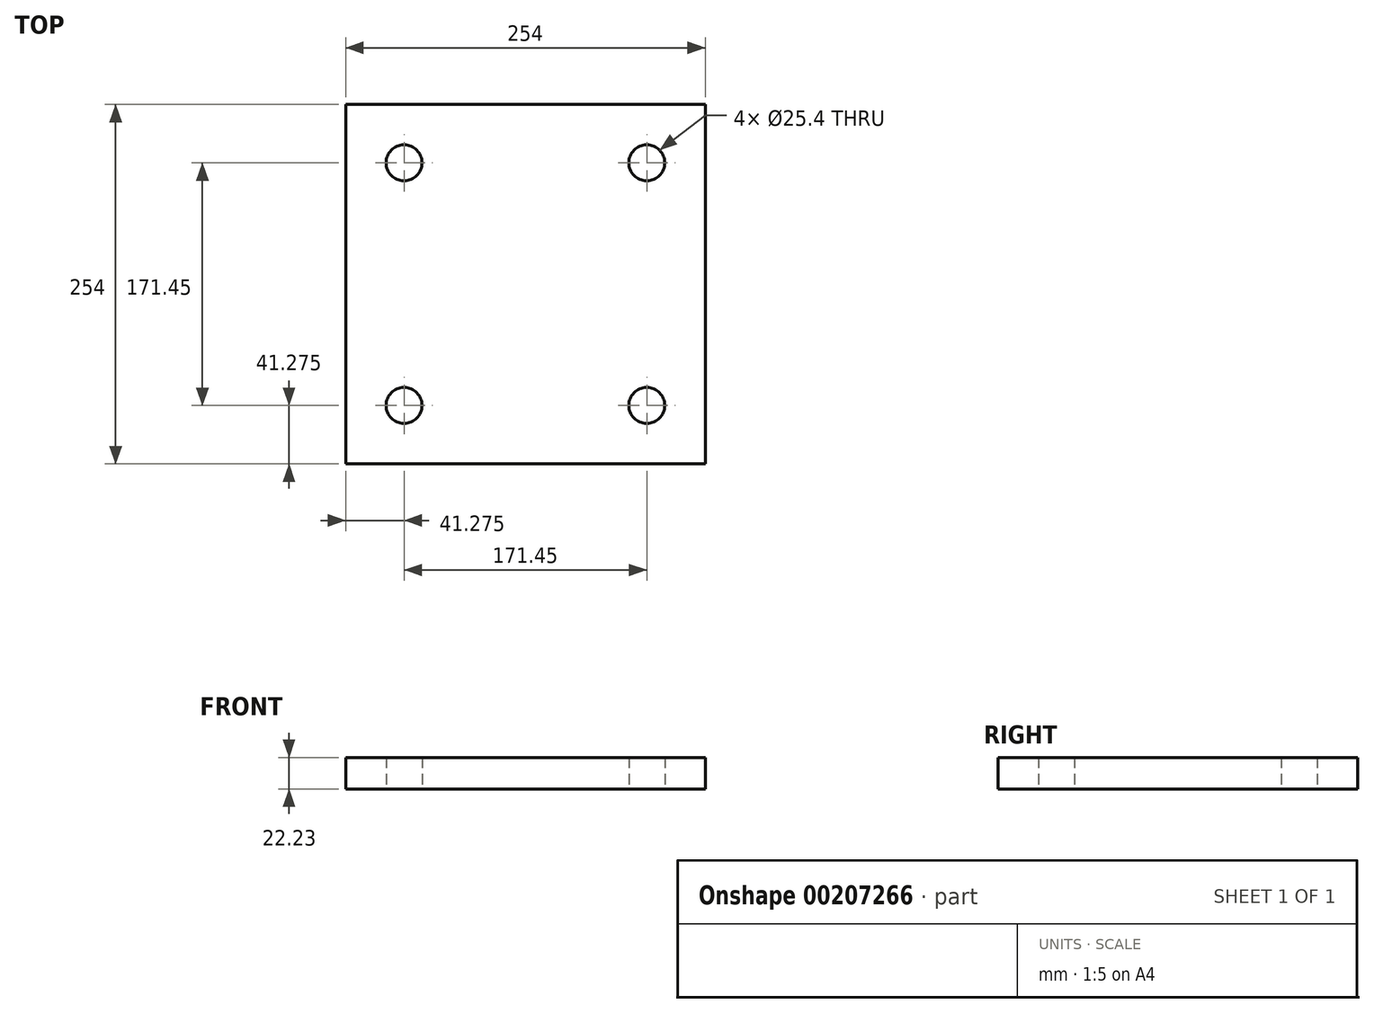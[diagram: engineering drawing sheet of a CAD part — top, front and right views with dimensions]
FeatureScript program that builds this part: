
annotation { "Feature Type Name" : "Feature", "Feature Type Description" : "" }
export const myFeature = defineFeature(function(context is Context, id is Id, definition is map)
    precondition{}
    {
        {
            var Q0;
            Q0=qCreatedBy(makeId("Top.planeOp"),FACE);
            var sketch = newSketch(context, id + "F0", { "sketchPlane" : qUnion([Q0])});
            skLineSegment(sketch, "E0.bottom", {"start": v(-127, 127) * mm, "end": v(127, 127) * mm});
            skLineSegment(sketch, "E0.top", {"start": v(-127, -127) * mm, "end": v(127, -127) * mm});
            skLineSegment(sketch, "E0.left", {"start": v(-127, 127) * mm, "end": v(-127, -127) * mm});
            skLineSegment(sketch, "E0.right", {"start": v(127, 127) * mm, "end": v(127, -127) * mm});
            skPoint(sketch, "E0.middle", {"position": v(0, 0) * mm});
            skCircle(sketch, "E1", {"center": v(-85.72, 85.72) * mm, "radius": 12.7 * mm});
            skCircle(sketch, "E2", {"center": v(85.73, 85.72) * mm, "radius": 12.7 * mm});
            skCircle(sketch, "E3", {"center": v(85.73, -85.72) * mm, "radius": 12.7 * mm});
            skCircle(sketch, "E4", {"center": v(-85.72, -85.72) * mm, "radius": 12.7 * mm});
            skSolve(sketch);
        }
        {
            var Q0;
            Q0=makeQuery(id+"F0.imprint","IMPRINT",FACE,{"disambiguationData":[TD([[makeQuery(id+"F0.imprint","IMPRINT",EDGE,{"derivedFrom":sQuery(id+"F0.wireOp",EDGE,"E0.bottom")}),-1.0]])]});
            extrude(context, id + "F1", {"entities" : qUnion([Q0]), "depth" : 22.22 * mm});
        }
    });
